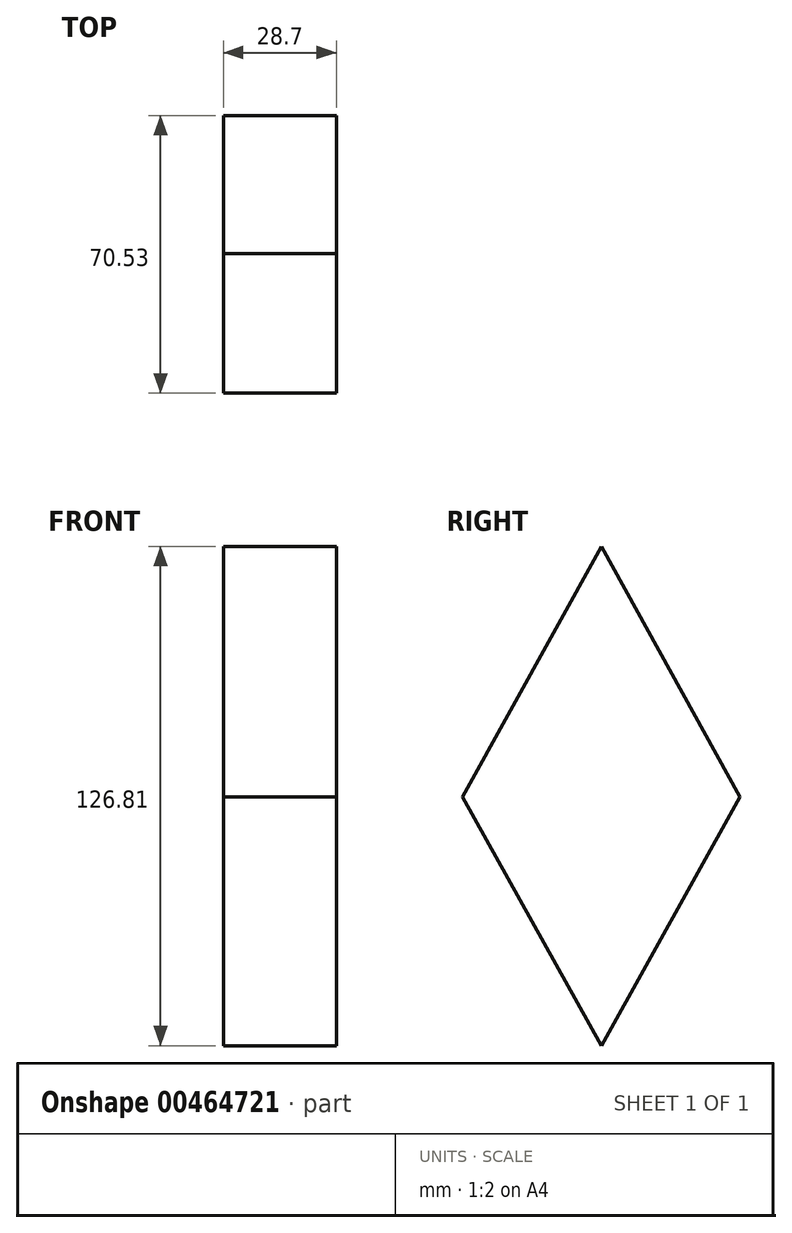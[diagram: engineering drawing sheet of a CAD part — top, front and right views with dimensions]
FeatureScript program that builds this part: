
annotation { "Feature Type Name" : "Feature", "Feature Type Description" : "" }
export const myFeature = defineFeature(function(context is Context, id is Id, definition is map)
    precondition{}
    {
        {
            var Q0;
            Q0=qCreatedBy(makeId("Right.planeOp"),FACE);
            var sketch = newSketch(context, id + "F0", { "sketchPlane" : qUnion([Q0])});
            skLineSegment(sketch, "E0", {"start": v(0, 0) * mm, "end": v(0, 63.6) * mm});
            skLineSegment(sketch, "E1", {"start": v(0, 63.6) * mm, "end": v(35.15, 0) * mm});
            skLineSegment(sketch, "E2", {"start": v(35.15, 0) * mm, "end": v(0, -63.2) * mm});
            skLineSegment(sketch, "E3", {"start": v(0, 0) * mm, "end": v(0, -63.2) * mm});
            skLineSegment(sketch, "E4", {"start": v(0, 63.6) * mm, "end": v(-35.38, 0) * mm});
            skLineSegment(sketch, "E5", {"start": v(-35.38, 0) * mm, "end": v(0, -63.2) * mm});
            skLineSegment(sketch, "E6", {"start": v(35.15, 0) * mm, "end": v(0, 0) * mm});
            skLineSegment(sketch, "E7", {"start": v(-35.38, 0) * mm, "end": v(0, 0) * mm});
            skSolve(sketch);
        }
        {
            var Q0;
            Q0=makeQuery(id+"F0.imprint","IMPRINT",FACE,{"disambiguationData":[TD([[makeQuery(id+"F0.imprint","IMPRINT",EDGE,{"derivedFrom":sQuery(id+"F0.wireOp",EDGE,"E0")}),-1.0]])]});
            var Q1;
            Q1=makeQuery(id+"F0.imprint","IMPRINT",FACE,{"disambiguationData":[TD([[makeQuery(id+"F0.imprint","IMPRINT",EDGE,{"derivedFrom":sQuery(id+"F0.wireOp",EDGE,"E0")}),1.0]])]});
            var Q2;
            Q2=makeQuery(id+"F0.imprint","IMPRINT",FACE,{"disambiguationData":[TD([[makeQuery(id+"F0.imprint","IMPRINT",EDGE,{"derivedFrom":sQuery(id+"F0.wireOp",EDGE,"E3")}),-1.0]])]});
            var Q3;
            Q3=makeQuery(id+"F0.imprint","IMPRINT",FACE,{"disambiguationData":[TD([[makeQuery(id+"F0.imprint","IMPRINT",EDGE,{"derivedFrom":sQuery(id+"F0.wireOp",EDGE,"E2")}),-1.0]])]});
            extrude(context, id + "F1", {"entities" : qUnion([Q0, Q1, Q2, Q3]), "depth" : 28.7 * mm});
        }
    });
